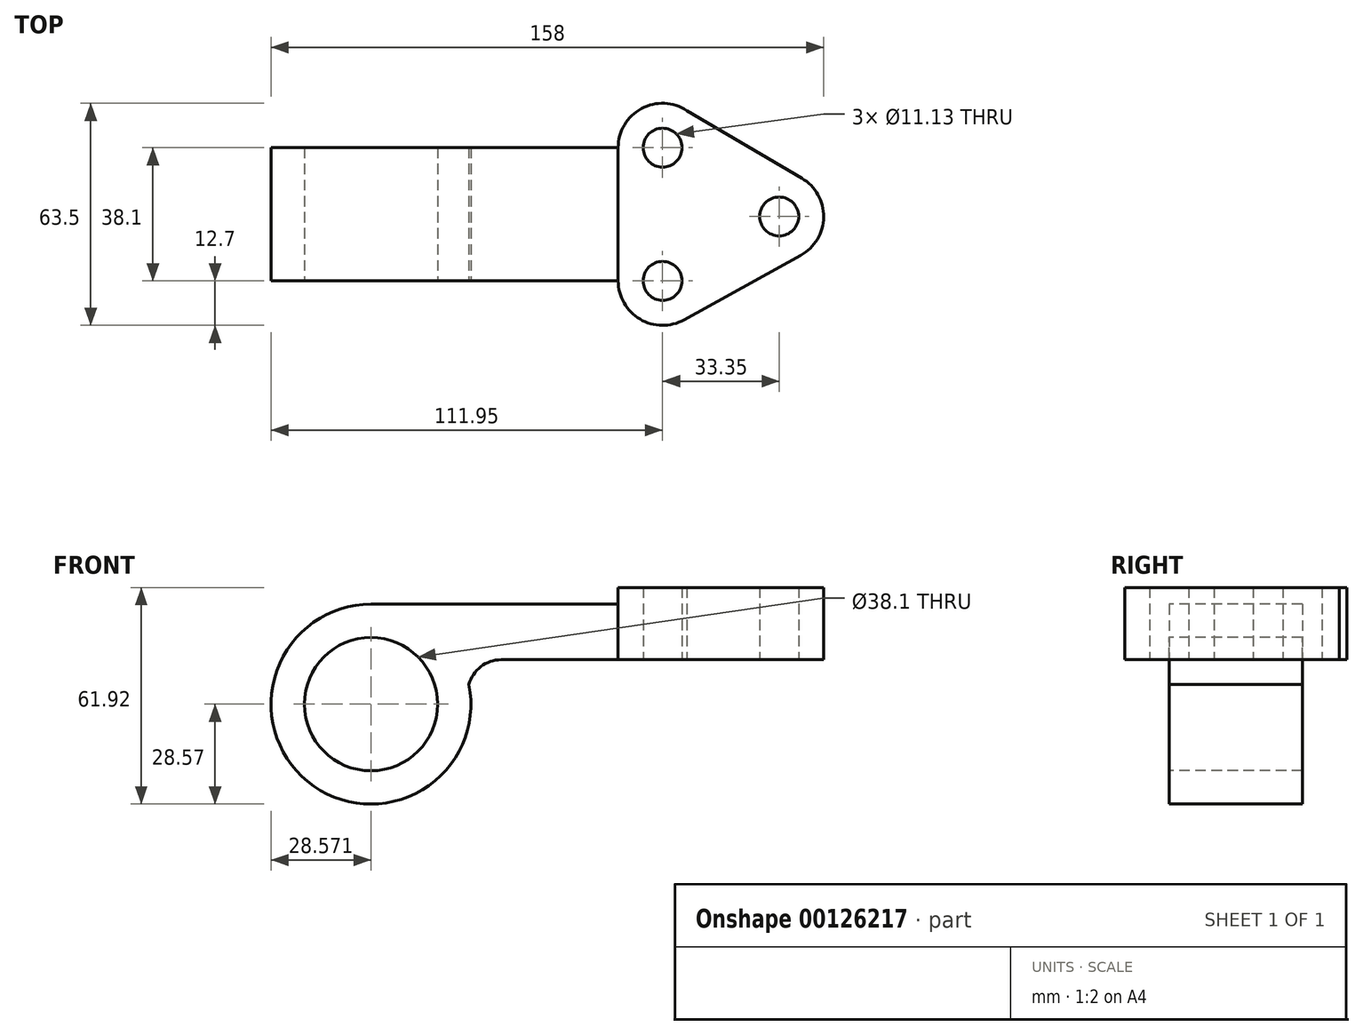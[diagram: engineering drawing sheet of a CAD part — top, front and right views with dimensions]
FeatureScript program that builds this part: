
annotation { "Feature Type Name" : "Feature", "Feature Type Description" : "" }
export const myFeature = defineFeature(function(context is Context, id is Id, definition is map)
    precondition{}
    {
        {
            var Q0;
            Q0=qCreatedBy(makeId("Top.planeOp"),FACE);
            var sketch = newSketch(context, id + "F0", { "sketchPlane" : qUnion([Q0])});
            skLineSegment(sketch, "E0", {"start": v(0, 0) * mm, "end": v(0, 38.1) * mm});
            skArc(sketch, "E1", {"start": v(19.67, 48.72) * mm, "mid": v(6.67, 49.28) * mm, "end": v(0, 38.1) * mm});
            skLineSegment(sketch, "E2", {"start": v(19.67, 48.72) * mm, "end": v(52.5, 29.38) * mm});
            skArc(sketch, "E3", {"start": v(52.19, 7.32) * mm, "mid": v(58.75, 18.26) * mm, "end": v(52.5, 29.38) * mm});
            skLineSegment(sketch, "E4", {"start": v(52.19, 7.32) * mm, "end": v(18.84, -11.11) * mm});
            skArc(sketch, "E5", {"start": v(0, 0) * mm, "mid": v(6.25, -10.94) * mm, "end": v(18.84, -11.11) * mm});
            skLineSegment(sketch, "E6", {"start": v(46.05, 18.44) * mm, "end": v(-79.74, 18.44) * mm, "construction": true});
            skCircle(sketch, "E7", {"center": v(12.7, 38.1) * mm, "radius": 5.56 * mm});
            skCircle(sketch, "E8", {"center": v(12.7, 0) * mm, "radius": 5.56 * mm});
            skCircle(sketch, "E9", {"center": v(46.05, 18.44) * mm, "radius": 5.56 * mm});
            skSolve(sketch);
        }
        {
            var Q0;
            Q0=makeQuery(id+"F0.imprint","IMPRINT",FACE,{"disambiguationData":[TD([[makeQuery(id+"F0.imprint","IMPRINT",EDGE,{"derivedFrom":sQuery(id+"F0.wireOp",EDGE,"E0")}),-1.0]])]});
            extrude(context, id + "F1", {"entities" : qUnion([Q0]), "depth" : 20.65 * mm});
        }
        {
            var Q0;
            Q0=qCreatedBy(makeId("Front.planeOp"),FACE);
            var sketch = newSketch(context, id + "F2", { "sketchPlane" : qUnion([Q0])});
            skLineSegment(sketch, "E10", {"start": v(0, 15.88) * mm, "end": v(-70.68, 15.87) * mm});
            skLineSegment(sketch, "E11", {"start": v(0, 0) * mm, "end": v(-33.45, 0) * mm});
            skPoint(sketch, "E12.visualSharp", {"position": v(-41.72, 0) * mm});
            skArc(sketch, "E12.filletArc", {"start": v(-33.45, 0) * mm, "mid": v(-39.26, -1.98) * mm, "end": v(-42.66, -7.1) * mm});
            skArc(sketch, "E13", {"start": v(-70.68, 15.87) * mm, "mid": v(-81.2, 13.87) * mm, "end": v(-90.25, 8.12) * mm});
            skArc(sketch, "E14", {"start": v(-90.25, 8.12) * mm, "mid": v(-79.38, -39.92) * mm, "end": v(-42.66, -7.1) * mm});
            skCircle(sketch, "E15", {"center": v(-70.68, -12.7) * mm, "radius": 19.05 * mm});
            skLineSegment(sketch, "E16", {"start": v(0, 15.88) * mm, "end": v(0, 0) * mm});
            skSolve(sketch);
        }
        {
            var Q0;
            Q0=makeQuery(id+"F2.imprint","IMPRINT",FACE,{"disambiguationData":[TD([[makeQuery(id+"F2.imprint","IMPRINT",EDGE,{"derivedFrom":sQuery(id+"F2.wireOp",EDGE,"E10")}),1.0]])]});
            extrude(context, id + "F3", {"entities" : qUnion([Q0]), "operationType" : NewBodyOperationType.ADD, "oppositeDirection" : true, "depth" : 38.1 * mm});
        }
    });
